# Revit family: Gira_126066
name_source: partatom
category: Electrical Fixtures
revit_build: Autodesk Revit 2017 (Build: 20160225_1515(x64)
units: mm (PartAtom-declared; Revit-internal decimal feet)

## family parameters
Cut with Voids When Loaded = No
Host = Face
Maintain Annotation Orientation = Yes
Part Type = Normal
Room Calculation Point = No
Round Connector Dimension = Use Diameter
Shared = No

## types (1)
- Door st. 1-g FM Gira TX_44 (WP FM) p.white
    Available = No
    BIM (1) = https://media.stage.bim.site und Tasten.rfa?public/gira/36a6b08/TX44_Komplettgerät_Schalten und Tasten.rfa
    Category = Door station door communication
    Colour = White
    Data sheet (1) = https://katalog.gira.de
    Default Elevation = 1219 mm
    Description = Door st.1g FM TX_44 PW,Door station, 1-gang,,pure white,Features:,- Installation in a conventional flush-mounted device box.,- Fits in the cover frames of the Gira TX_44 switch range.,- Modular design, therefore easy installation and expandability with further components such as call buttons, info module, colour camera, Keyless In.,- Signal transmission and supply of the audio and video components via reverse-polarity-protected and short-circuit-proof 2-wire bus.,- One-man start-up with easy start-up procedure.,- Weather-resistant speaker.,- High-quality electret microphone.,- Speakerphone function (voice-controlled talk-back with echo and background noise suppression).,- Call button LED lamps, white light. Even, clearly visible call-button illumination is achieved via maintenance-free, energy-saving LED technology.,- Audible acknowledgement signal when a call button is pressed.,- Adjustable voice volume.,- Sprayed-water proof call-button cover plate made of shock-resistant plastic.,- Name plate of the call button can be exchanged without tools and without frame disassembly.,- Professional labelling is available from the Gira Inscription Service www.marking.gira.com or using the Gira inscription software.,- Binary input for connecting a zero-voltage push button (NO contact) as a call button.,- Call button, 1-gang
    GTIN = 4010337260660
    HAN = 126066
    HeinzeBIM = https://bimportal.heinze.de
    Installation technique = Bus system
    Manufacturer = Gira
    Manufacturer URL = https://www.gira.de
    Modular construction = Yes
    Mounting method = Flush mounted (plaster)
    Name = Door st. 1-g FM Gira TX_44 (WP FM) p.white
    Number of call buttons = 1
    Protection against vandalism = Yes
    URL = http://katalog.gira.de
    With camera = No
    With cover = Yes
    With info label = Yes

## geometry (parser evidence)
native form markers: Sweep x2
no freeform markers — native parametric forms only
